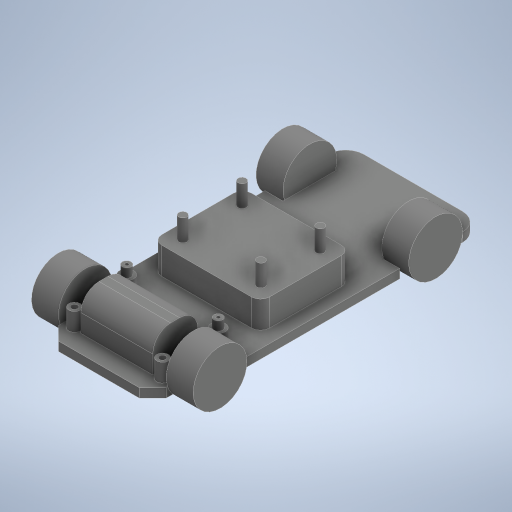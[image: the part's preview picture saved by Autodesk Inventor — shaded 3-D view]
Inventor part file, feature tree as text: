
AUTODESK INVENTOR PART (.ipt)
format: ipt  version: 2024.2 (Build 282272000, 272)  size: 465,920 bytes
history: native  units: mm
features: extrude x11, sketch x11, projected_geometry x5, fillet x2, mirror x2, plane x1
ambient origin geometry x8: Origin, YZ Plane, XZ Plane, XY Plane, X Axis, Y Axis, Z Axis, Center Point
bodies: Body1 (feature_tree)
feature tree (32):
  extrude  "Extrusion5"  Depth=175.0mm
  extrude  "Extrusion6"  Depth=15.0mm
  extrude  "Extrusion7"  Depth=15.0mm
  fillet  "Fillet2"  Radius=10.0mm
  extrude  "Extrusion8"  Depth=10.0mm
  plane  "Work Plane1"
  mirror  "Mirror1"
  extrude  "Extrusion9"  Depth=15.0mm
  mirror  "Mirror2"
  fillet  "Fillet3"  Radius=30.0mm
  extrude  "Extrusion10"  Depth=60.0mm
  extrude  "Extrusion11"  Depth=7.5mm
  extrude  "Extrusion12"  Depth=15.0mm TaperAngle=0.0deg
  extrude  "Extrusion13"  Depth=40.0mm
  extrude  "Extrusion14"  Depth=10.0mm
  extrude  "Extrusion15"  Depth=10.0mm
  sketch  "Sketch6"  dims[d30=75.0mm d31=175.0mm]
  sketch  "Sketch7"  dims[d32=15.0mm d33=15.0mm]
  sketch  "Sketch8"  dims[d34=15.0mm d35=15.0mm d36=10.0mm]
  sketch  "Sketch9"  dims[d37=40.0mm d38=10.0mm]
  sketch  "Sketch10"  dims[d39=10.0mm d40=15.0mm d41=30.0mm]
  sketch  "Sketch12"  dims[d42=5.0mm d43=0.0mm d44=60.0mm]
  sketch  "Sketch14"  dims[d45=50.0mm d46=7.5mm]
  sketch  "Sketch15"  dims[d47=20.0mm d48=15.0mm d49=0.0mm]
  projected_geometry  "Projected Loop1"
  projected_geometry  "Projected Loop2"
  projected_geometry  "Projected Loop3"
  sketch  "Sketch16"  dims[d50=25.0mm d51=40.0mm]
  sketch  "Sketch18"  dims[d52=10.0mm d53=10.0mm]
  projected_geometry  "Projected Loop4"
  projected_geometry  "Projected Loop5"
  sketch  "Sketch19"  dims[d54=20.0mm d55=0.0mm d56=10.0mm d57=30.0mm d58=15.0mm d59=10.0mm d63=15.0mm d64=0.0mm d65=-37.5mm d66=30.0mm d67=15.0mm d68=10.0mm d69=15.0mm d70=0.0mm d71=5.0mm d72=4.5mm d73=4.5mm d74=4.5mm d75=4.5mm d76=43.5mm d77=33.0mm d78=8.5mm d79=8.25mm d80=12.0mm d81=0.0mm d82=51.0mm d83=12.0mm d84=1.0mm d85=8.0mm d86=8.0mm d87=49.0mm d88=1.0mm d89=6.5mm d90=6.5mm d91=30.0mm d92=5.0mm d93=0.0mm d94=5.0mm d95=5.0mm d96=3.5mm d97=3.5mm d98=5.0mm d99=0.0mm d100=5.0mm d101=5.0mm d102=5.0mm d103=0.0mm d104=2.0mm d105=2.0mm d106=0.0mm d107=0.0mm d108=3.5mm d109=3.5mm d110=8.0mm d111=0.0mm]
